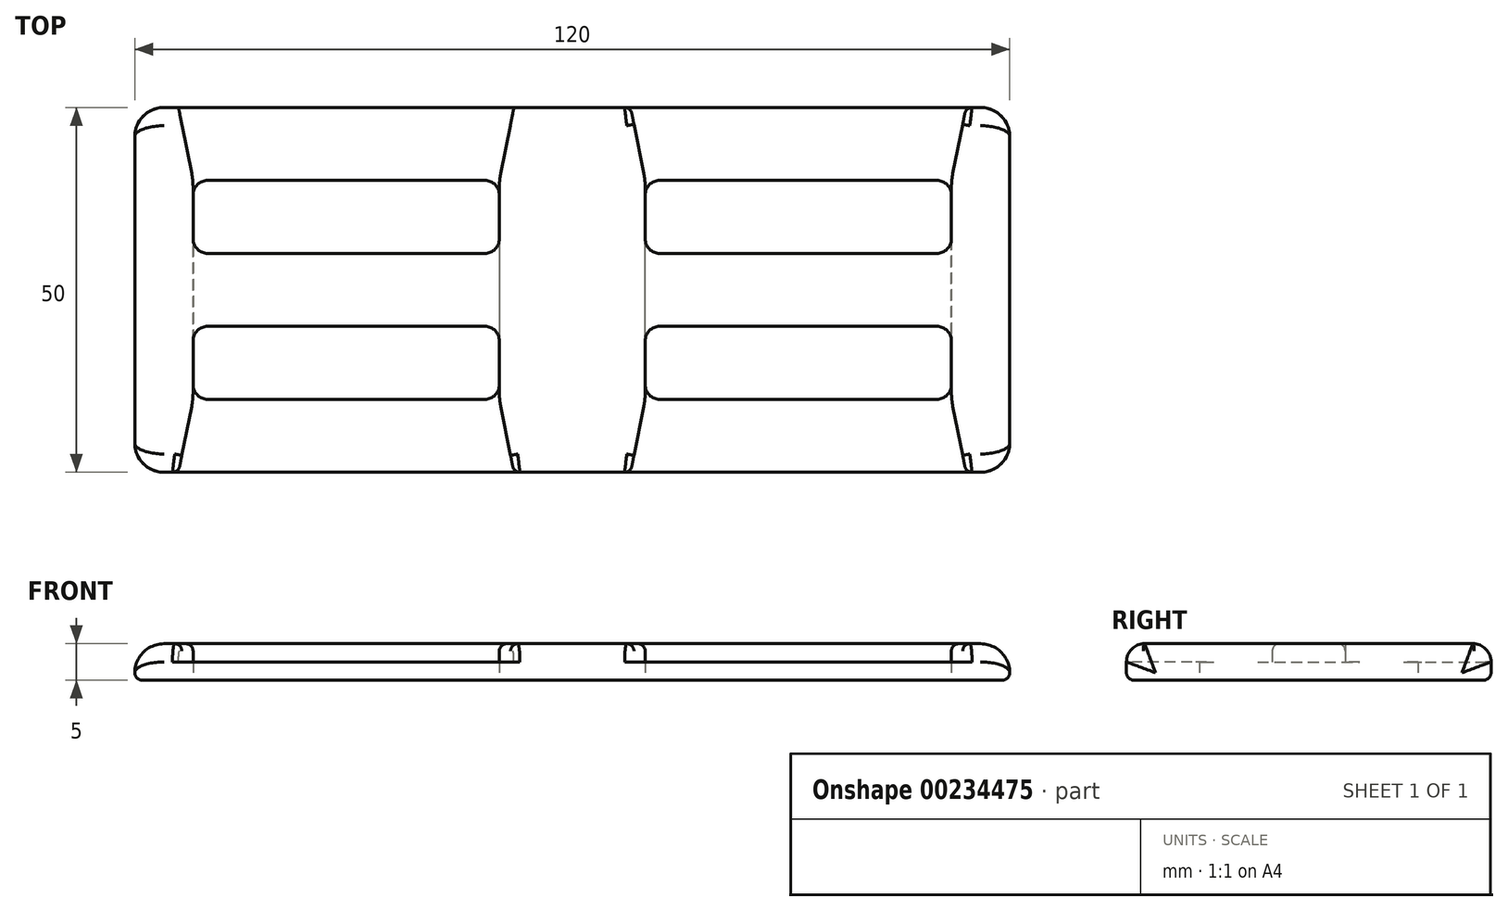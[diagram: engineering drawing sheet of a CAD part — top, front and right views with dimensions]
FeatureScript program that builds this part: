
annotation { "Feature Type Name" : "Feature", "Feature Type Description" : "" }
export const myFeature = defineFeature(function(context is Context, id is Id, definition is map)
    precondition{}
    {
        {
            var Q0;
            Q0=qCreatedBy(makeId("Top.planeOp"),FACE);
            var sketch = newSketch(context, id + "F0", { "sketchPlane" : qUnion([Q0])});
            skLineSegment(sketch, "E0.bottom", {"start": v(-60, 25) * mm, "end": v(60, 25) * mm});
            skLineSegment(sketch, "E0.top", {"start": v(-60, -25) * mm, "end": v(60, -25) * mm});
            skLineSegment(sketch, "E0.left", {"start": v(-60, 25) * mm, "end": v(-60, -25) * mm});
            skLineSegment(sketch, "E0.right", {"start": v(60, 25) * mm, "end": v(60, -25) * mm});
            skPoint(sketch, "E0.middle", {"position": v(0, 0) * mm});
            skLineSegment(sketch, "E1.bottom", {"start": v(-52, 15) * mm, "end": v(-10, 15) * mm});
            skLineSegment(sketch, "E1.top", {"start": v(-52, 5) * mm, "end": v(-10, 5) * mm});
            skLineSegment(sketch, "E1.left", {"start": v(-52, 15) * mm, "end": v(-52, 5) * mm});
            skLineSegment(sketch, "E1.right", {"start": v(-10, 15) * mm, "end": v(-10, 5) * mm});
            skLineSegment(sketch, "E2.MirrorCS", {"start": v(52, 15) * mm, "end": v(52, 5) * mm});
            skLineSegment(sketch, "E3.MirrorCS", {"start": v(52, 15) * mm, "end": v(10, 15) * mm});
            skLineSegment(sketch, "E4.MirrorCS", {"start": v(52, 5) * mm, "end": v(10, 5) * mm});
            skLineSegment(sketch, "E5.MirrorCS", {"start": v(10, 15) * mm, "end": v(10, 5) * mm});
            skLineSegment(sketch, "E6.MirrorCS", {"start": v(-52, -5) * mm, "end": v(-10, -5) * mm});
            skLineSegment(sketch, "E7.MirrorCS", {"start": v(10, -15) * mm, "end": v(10, -5) * mm});
            skLineSegment(sketch, "E8.MirrorCS", {"start": v(-52, -15) * mm, "end": v(-10, -15) * mm});
            skLineSegment(sketch, "E9.MirrorCS", {"start": v(52, -5) * mm, "end": v(10, -5) * mm});
            skLineSegment(sketch, "E10.MirrorCS", {"start": v(-52, -15) * mm, "end": v(-52, -5) * mm});
            skLineSegment(sketch, "E11.MirrorCS", {"start": v(52, -15) * mm, "end": v(10, -15) * mm});
            skLineSegment(sketch, "E12.MirrorCS", {"start": v(-10, -15) * mm, "end": v(-10, -5) * mm});
            skLineSegment(sketch, "E13.MirrorCS", {"start": v(52, -15) * mm, "end": v(52, -5) * mm});
            skSolve(sketch);
        }
        {
            var Q0;
            Q0 = qSketchRegion(id + "F0", true);
            extrude(context, id + "F1", {"entities" : qUnion([Q0]), "depth" : 5 * mm, "offsetDistance" : 25 * mm});
        }
        {
            var Q0;
            Q0=makeQuery(id+"F1.opExtrude","CAP_FACE",FACE,{"disambiguationData":[OSD([sQuery(id+"F0.wireOp",EDGE,"E0.bottom"),sQuery(id+"F0.wireOp",EDGE,"E0.top"),sQuery(id+"F0.wireOp",EDGE,"E0.left"),sQuery(id+"F0.wireOp",EDGE,"E0.right"),sQuery(id+"F0.wireOp",EDGE,"E1.bottom"),sQuery(id+"F0.wireOp",EDGE,"E1.top"),sQuery(id+"F0.wireOp",EDGE,"E1.left"),sQuery(id+"F0.wireOp",EDGE,"E1.right"),sQuery(id+"F0.wireOp",EDGE,"E2.MirrorCS"),sQuery(id+"F0.wireOp",EDGE,"E3.MirrorCS"),sQuery(id+"F0.wireOp",EDGE,"E4.MirrorCS"),sQuery(id+"F0.wireOp",EDGE,"E5.MirrorCS"),sQuery(id+"F0.wireOp",EDGE,"E6.MirrorCS"),sQuery(id+"F0.wireOp",EDGE,"E7.MirrorCS"),sQuery(id+"F0.wireOp",EDGE,"E8.MirrorCS"),sQuery(id+"F0.wireOp",EDGE,"E9.MirrorCS"),sQuery(id+"F0.wireOp",EDGE,"E10.MirrorCS"),sQuery(id+"F0.wireOp",EDGE,"E11.MirrorCS"),sQuery(id+"F0.wireOp",EDGE,"E12.MirrorCS"),sQuery(id+"F0.wireOp",EDGE,"E13.MirrorCS")])],"isStart":false});
            var sketch = newSketch(context, id + "F2", { "sketchPlane" : qUnion([Q0])});
            skLineSegment(sketch, "E14.0", {"start": v(-52, 15) * mm, "end": v(-10, 15) * mm});
            skLineSegment(sketch, "E15.0", {"start": v(-54, 25) * mm, "end": v(-8, 25) * mm});
            skLineSegment(sketch, "E16", {"start": v(-52, 15) * mm, "end": v(-54, 25) * mm});
            skLineSegment(sketch, "E17", {"start": v(-10, 15) * mm, "end": v(-8, 25) * mm});
            skLineSegment(sketch, "E18", {"start": v(-31, 15) * mm, "end": v(-31, 25) * mm, "construction": true});
            skPoint(sketch, "E19.orphan", {"position": v(60, 25) * mm});
            skPoint(sketch, "E20.orphan", {"position": v(-60, 25) * mm});
            skLineSegment(sketch, "E21.MirrorCS", {"start": v(54, 25) * mm, "end": v(8, 25) * mm});
            skLineSegment(sketch, "E22.MirrorCS", {"start": v(52, 15) * mm, "end": v(54, 25) * mm});
            skLineSegment(sketch, "E23.MirrorCS", {"start": v(52, 15) * mm, "end": v(10, 15) * mm});
            skLineSegment(sketch, "E24.MirrorCS", {"start": v(10, 15) * mm, "end": v(8, 25) * mm});
            skLineSegment(sketch, "E25.MirrorCS", {"start": v(31, 15) * mm, "end": v(31, 25) * mm, "construction": true});
            skLineSegment(sketch, "E26.MirrorCS", {"start": v(52, -15) * mm, "end": v(10, -15) * mm});
            skLineSegment(sketch, "E27.MirrorCS", {"start": v(-52, -15) * mm, "end": v(-54, -25) * mm});
            skLineSegment(sketch, "E28.MirrorCS", {"start": v(54, -25) * mm, "end": v(8, -25) * mm});
            skLineSegment(sketch, "E29.MirrorCS", {"start": v(10, -15) * mm, "end": v(8, -25) * mm});
            skPoint(sketch, "E30.MirrorP", {"position": v(60, -25) * mm});
            skLineSegment(sketch, "E31.MirrorCS", {"start": v(-54, -25) * mm, "end": v(-8, -25) * mm});
            skLineSegment(sketch, "E32.MirrorCS", {"start": v(-10, -15) * mm, "end": v(-8, -25) * mm});
            skLineSegment(sketch, "E33.MirrorCS", {"start": v(52, -15) * mm, "end": v(54, -25) * mm});
            skPoint(sketch, "E34.MirrorP", {"position": v(-60, -25) * mm});
            skLineSegment(sketch, "E35.MirrorCS", {"start": v(-52, -15) * mm, "end": v(-10, -15) * mm});
            skLineSegment(sketch, "E36.MirrorCS", {"start": v(-31, -15) * mm, "end": v(-31, -25) * mm, "construction": true});
            skLineSegment(sketch, "E37.MirrorCS", {"start": v(31, -15) * mm, "end": v(31, -25) * mm, "construction": true});
            skSolve(sketch);
        }
        {
            var Q0;
            Q0=qCreatedBy(makeId("Top.planeOp"),FACE);
            var sketch = newSketch(context, id + "F3", { "sketchPlane" : qUnion([Q0])});
            skLineSegment(sketch, "E38.0", {"start": v(-52, 5) * mm, "end": v(-10, 5) * mm});
            skLineSegment(sketch, "E39.0", {"start": v(-52, -5) * mm, "end": v(-10, -5) * mm});
            skLineSegment(sketch, "E40.0", {"start": v(52, -5) * mm, "end": v(10, -5) * mm});
            skLineSegment(sketch, "E41.0", {"start": v(52, 5) * mm, "end": v(10, 5) * mm});
            skLineSegment(sketch, "E42", {"start": v(-52, -5) * mm, "end": v(-52, 5) * mm});
            skLineSegment(sketch, "E43", {"start": v(-10, 5) * mm, "end": v(-10, -5) * mm});
            skLineSegment(sketch, "E44", {"start": v(10, -5) * mm, "end": v(10, 5) * mm});
            skLineSegment(sketch, "E45", {"start": v(52, 5) * mm, "end": v(52, -5) * mm});
            skSolve(sketch);
        }
        {
            var Q0;
            Q0 = qSketchRegion(id + "F2", true);
            extrude(context, id + "F4", {"entities" : qUnion([Q0]), "operationType" : NewBodyOperationType.REMOVE, "oppositeDirection" : true, "depth" : 2.5 * mm, "offsetDistance" : 25 * mm});
        }
        {
            var Q0;
            Q0 = qSketchRegion(id + "F3", true);
            extrude(context, id + "F5", {"entities" : qUnion([Q0]), "operationType" : NewBodyOperationType.REMOVE, "depth" : 2.5 * mm, "offsetDistance" : 25 * mm});
        }
        {
            var Q0;
            {var subQ0=sQuery(id+"F0.wireOp",EDGE,"E0.bottom");var subQ1=sQuery(id+"F0.wireOp",EDGE,"E0.right");Q0=makeQuery(id+"F4.boolean.opBoolean","SPLIT",EDGE,{"disambiguationData":[TD([makeQuery(id+"F1.opExtrude","SWEPT_FACE",FACE,{"disambiguationData":[OSD([subQ1])]})])],"derivedFrom":makeQuery(id+"F1.opExtrude","CAP_EDGE",EDGE,{"disambiguationData":[OSD([subQ0])],"isStart":false})});}
            var Q1;
            {var subQ0=sQuery(id+"F0.wireOp",EDGE,"E0.bottom");Q1=makeQuery(id+"F4.boolean.opBoolean","SPLIT",EDGE,{"disambiguationData":[TD([makeQuery(id+"F4.opExtrude","SWEPT_FACE",FACE,{"disambiguationData":[OSD([sQuery(id+"F2.wireOp",EDGE,"E17")])]})])],"derivedFrom":makeQuery(id+"F1.opExtrude","CAP_EDGE",EDGE,{"disambiguationData":[OSD([subQ0])],"isStart":false})});}
            var Q2;
            {var subQ0=sQuery(id+"F0.wireOp",EDGE,"E0.bottom");var subQ1=sQuery(id+"F0.wireOp",EDGE,"E0.left");Q2=makeQuery(id+"F4.boolean.opBoolean","SPLIT",EDGE,{"disambiguationData":[TD([makeQuery(id+"F1.opExtrude","SWEPT_FACE",FACE,{"disambiguationData":[OSD([subQ1])]})])],"derivedFrom":makeQuery(id+"F1.opExtrude","CAP_EDGE",EDGE,{"disambiguationData":[OSD([subQ0])],"isStart":false})});}
            var Q3;
            {var subQ0=sQuery(id+"F0.wireOp",EDGE,"E0.left");var subQ1=sQuery(id+"F0.wireOp",EDGE,"E0.top");Q3=makeQuery(id+"F4.boolean.opBoolean","SPLIT",EDGE,{"disambiguationData":[TD([makeQuery(id+"F1.opExtrude","SWEPT_FACE",FACE,{"disambiguationData":[OSD([subQ0])]})])],"derivedFrom":makeQuery(id+"F1.opExtrude","CAP_EDGE",EDGE,{"disambiguationData":[OSD([subQ1])],"isStart":false})});}
            var Q4;
            {var subQ0=sQuery(id+"F0.wireOp",EDGE,"E0.top");Q4=makeQuery(id+"F4.boolean.opBoolean","SPLIT",EDGE,{"disambiguationData":[TD([makeQuery(id+"F4.opExtrude","SWEPT_FACE",FACE,{"disambiguationData":[OSD([sQuery(id+"F2.wireOp",EDGE,"E29.MirrorCS")])]})])],"derivedFrom":makeQuery(id+"F1.opExtrude","CAP_EDGE",EDGE,{"disambiguationData":[OSD([subQ0])],"isStart":false})});}
            var Q5;
            {var subQ0=sQuery(id+"F0.wireOp",EDGE,"E0.right");var subQ1=sQuery(id+"F0.wireOp",EDGE,"E0.top");Q5=makeQuery(id+"F4.boolean.opBoolean","SPLIT",EDGE,{"disambiguationData":[TD([makeQuery(id+"F1.opExtrude","SWEPT_FACE",FACE,{"disambiguationData":[OSD([subQ0])]})])],"derivedFrom":makeQuery(id+"F1.opExtrude","CAP_EDGE",EDGE,{"disambiguationData":[OSD([subQ1])],"isStart":false})});}
            fillet(context, id + "F6", {"entities" : qUnion([Q0, Q1, Q2, Q3, Q4, Q5]), "tangentPropagation" : true, "radius" : 2.5 * mm, "defaultsChanged" : false, "vertexSettings" : [], "allowEdgeOverflow" : false});
        }
        {
            var Q0;
            Q0=makeQuery(id+"F1.opExtrude","CAP_EDGE",EDGE,{"disambiguationData":[OSD([sQuery(id+"F0.wireOp",EDGE,"E0.right")])],"isStart":false});
            var Q1;
            Q1=makeQuery(id+"F1.opExtrude","CAP_EDGE",EDGE,{"disambiguationData":[OSD([sQuery(id+"F0.wireOp",EDGE,"E0.left")])],"isStart":false});
            fillet(context, id + "F7", {"entities" : qUnion([Q0, Q1]), "tangentPropagation" : true, "radius" : 4 * mm, "defaultsChanged" : false, "vertexSettings" : [], "allowEdgeOverflow" : false});
        }
        {
            var Q0;
            Q0=makeQuery(id+"F1.opExtrude","SWEPT_EDGE",EDGE,{"disambiguationData":[OSD([sQuery(id+"F0.wireOp",EDGE,"E2.MirrorCS"),sQuery(id+"F0.wireOp",EDGE,"E4.MirrorCS")])]});
            var Q1;
            Q1=makeQuery(id+"F1.opExtrude","SWEPT_EDGE",EDGE,{"disambiguationData":[OSD([sQuery(id+"F0.wireOp",EDGE,"E4.MirrorCS"),sQuery(id+"F0.wireOp",EDGE,"E5.MirrorCS")])]});
            var Q2;
            Q2=makeQuery(id+"F1.opExtrude","SWEPT_EDGE",EDGE,{"disambiguationData":[OSD([sQuery(id+"F0.wireOp",EDGE,"E1.top"),sQuery(id+"F0.wireOp",EDGE,"E1.right")])]});
            var Q3;
            Q3=makeQuery(id+"F1.opExtrude","SWEPT_EDGE",EDGE,{"disambiguationData":[OSD([sQuery(id+"F0.wireOp",EDGE,"E1.top"),sQuery(id+"F0.wireOp",EDGE,"E1.left")])]});
            var Q4;
            Q4=makeQuery(id+"F4.boolean.opBoolean","SPLIT",EDGE,{"derivedFrom":makeQuery(id+"F1.opExtrude","SWEPT_EDGE",EDGE,{"disambiguationData":[OSD([sQuery(id+"F0.wireOp",EDGE,"E8.MirrorCS"),sQuery(id+"F0.wireOp",EDGE,"E10.MirrorCS")])]})});
            var Q5;
            Q5=makeQuery(id+"F4.boolean.opBoolean","SPLIT",EDGE,{"derivedFrom":makeQuery(id+"F1.opExtrude","SWEPT_EDGE",EDGE,{"disambiguationData":[OSD([sQuery(id+"F0.wireOp",EDGE,"E8.MirrorCS"),sQuery(id+"F0.wireOp",EDGE,"E12.MirrorCS")])]})});
            var Q6;
            Q6=makeQuery(id+"F4.boolean.opBoolean","SPLIT",EDGE,{"derivedFrom":makeQuery(id+"F1.opExtrude","SWEPT_EDGE",EDGE,{"disambiguationData":[OSD([sQuery(id+"F0.wireOp",EDGE,"E11.MirrorCS"),sQuery(id+"F0.wireOp",EDGE,"E13.MirrorCS")])]})});
            var Q7;
            Q7=makeQuery(id+"F4.boolean.opBoolean","SPLIT",EDGE,{"derivedFrom":makeQuery(id+"F1.opExtrude","SWEPT_EDGE",EDGE,{"disambiguationData":[OSD([sQuery(id+"F0.wireOp",EDGE,"E7.MirrorCS"),sQuery(id+"F0.wireOp",EDGE,"E11.MirrorCS")])]})});
            var Q8;
            Q8=makeQuery(id+"F1.opExtrude","SWEPT_EDGE",EDGE,{"disambiguationData":[OSD([sQuery(id+"F0.wireOp",EDGE,"E6.MirrorCS"),sQuery(id+"F0.wireOp",EDGE,"E12.MirrorCS")])]});
            var Q9;
            Q9=makeQuery(id+"F1.opExtrude","SWEPT_EDGE",EDGE,{"disambiguationData":[OSD([sQuery(id+"F0.wireOp",EDGE,"E6.MirrorCS"),sQuery(id+"F0.wireOp",EDGE,"E10.MirrorCS")])]});
            var Q10;
            Q10=makeQuery(id+"F1.opExtrude","SWEPT_EDGE",EDGE,{"disambiguationData":[OSD([sQuery(id+"F0.wireOp",EDGE,"E7.MirrorCS"),sQuery(id+"F0.wireOp",EDGE,"E9.MirrorCS")])]});
            var Q11;
            Q11=makeQuery(id+"F1.opExtrude","SWEPT_EDGE",EDGE,{"disambiguationData":[OSD([sQuery(id+"F0.wireOp",EDGE,"E9.MirrorCS"),sQuery(id+"F0.wireOp",EDGE,"E13.MirrorCS")])]});
            var Q12;
            Q12=makeQuery(id+"F4.boolean.opBoolean","SPLIT",EDGE,{"derivedFrom":makeQuery(id+"F1.opExtrude","SWEPT_EDGE",EDGE,{"disambiguationData":[OSD([sQuery(id+"F0.wireOp",EDGE,"E2.MirrorCS"),sQuery(id+"F0.wireOp",EDGE,"E3.MirrorCS")])]})});
            var Q13;
            Q13=makeQuery(id+"F4.boolean.opBoolean","SPLIT",EDGE,{"derivedFrom":makeQuery(id+"F1.opExtrude","SWEPT_EDGE",EDGE,{"disambiguationData":[OSD([sQuery(id+"F0.wireOp",EDGE,"E3.MirrorCS"),sQuery(id+"F0.wireOp",EDGE,"E5.MirrorCS")])]})});
            var Q14;
            Q14=makeQuery(id+"F4.boolean.opBoolean","SPLIT",EDGE,{"derivedFrom":makeQuery(id+"F1.opExtrude","SWEPT_EDGE",EDGE,{"disambiguationData":[OSD([sQuery(id+"F0.wireOp",EDGE,"E1.bottom"),sQuery(id+"F0.wireOp",EDGE,"E1.left")])]})});
            var Q15;
            Q15=makeQuery(id+"F4.boolean.opBoolean","SPLIT",EDGE,{"derivedFrom":makeQuery(id+"F1.opExtrude","SWEPT_EDGE",EDGE,{"disambiguationData":[OSD([sQuery(id+"F0.wireOp",EDGE,"E1.bottom"),sQuery(id+"F0.wireOp",EDGE,"E1.right")])]})});
            fillet(context, id + "F8", {"entities" : qUnion([Q0, Q1, Q2, Q3, Q4, Q5, Q6, Q7, Q8, Q9, Q10, Q11, Q12, Q13, Q14, Q15]), "tangentPropagation" : true, "radius" : 2 * mm, "defaultsChanged" : false, "vertexSettings" : [], "allowEdgeOverflow" : false});
        }
        {
            var Q0;
            {var subQ0=sQuery(id+"F0.wireOp",EDGE,"E2.MirrorCS");Q0=makeQuery(id+"F4.boolean.opBoolean","MERGE",EDGE,{"derivedFrom":[makeQuery(id+"F1.opExtrude","SWEPT_EDGE",EDGE,{"disambiguationData":[OSD([subQ0,sQuery(id+"F0.wireOp",EDGE,"E3.MirrorCS")])]})],"fromTools":[makeQuery(id+"F4.opExtrude","SWEPT_EDGE",EDGE,{"disambiguationData":[OSD([subQ0,sQuery(id+"F2.wireOp",EDGE,"E22.MirrorCS"),sQuery(id+"F2.wireOp",EDGE,"E23.MirrorCS")])]})]});}
            var Q1;
            {var subQ0=sQuery(id+"F0.wireOp",EDGE,"E5.MirrorCS");Q1=makeQuery(id+"F4.boolean.opBoolean","MERGE",EDGE,{"derivedFrom":[makeQuery(id+"F1.opExtrude","SWEPT_EDGE",EDGE,{"disambiguationData":[OSD([sQuery(id+"F0.wireOp",EDGE,"E3.MirrorCS"),subQ0])]})],"fromTools":[makeQuery(id+"F4.opExtrude","SWEPT_EDGE",EDGE,{"disambiguationData":[OSD([subQ0,sQuery(id+"F2.wireOp",EDGE,"E23.MirrorCS"),sQuery(id+"F2.wireOp",EDGE,"E24.MirrorCS")])]})]});}
            var Q2;
            {var subQ0=sQuery(id+"F0.wireOp",EDGE,"E1.right");Q2=makeQuery(id+"F4.boolean.opBoolean","MERGE",EDGE,{"derivedFrom":[makeQuery(id+"F1.opExtrude","SWEPT_EDGE",EDGE,{"disambiguationData":[OSD([sQuery(id+"F0.wireOp",EDGE,"E1.bottom"),subQ0])]})],"fromTools":[makeQuery(id+"F4.opExtrude","SWEPT_EDGE",EDGE,{"disambiguationData":[OSD([subQ0,sQuery(id+"F2.wireOp",EDGE,"E14.0"),sQuery(id+"F2.wireOp",EDGE,"E17")])]})]});}
            var Q3;
            {var subQ0=sQuery(id+"F0.wireOp",EDGE,"E1.left");Q3=makeQuery(id+"F4.boolean.opBoolean","MERGE",EDGE,{"derivedFrom":[makeQuery(id+"F1.opExtrude","SWEPT_EDGE",EDGE,{"disambiguationData":[OSD([sQuery(id+"F0.wireOp",EDGE,"E1.bottom"),subQ0])]})],"fromTools":[makeQuery(id+"F4.opExtrude","SWEPT_EDGE",EDGE,{"disambiguationData":[OSD([subQ0,sQuery(id+"F2.wireOp",EDGE,"E14.0"),sQuery(id+"F2.wireOp",EDGE,"E16")])]})]});}
            var Q4;
            {var subQ0=sQuery(id+"F0.wireOp",EDGE,"E10.MirrorCS");Q4=makeQuery(id+"F4.boolean.opBoolean","MERGE",EDGE,{"derivedFrom":[makeQuery(id+"F1.opExtrude","SWEPT_EDGE",EDGE,{"disambiguationData":[OSD([sQuery(id+"F0.wireOp",EDGE,"E8.MirrorCS"),subQ0])]})],"fromTools":[makeQuery(id+"F4.opExtrude","SWEPT_EDGE",EDGE,{"disambiguationData":[OSD([subQ0,sQuery(id+"F2.wireOp",EDGE,"E27.MirrorCS"),sQuery(id+"F2.wireOp",EDGE,"E35.MirrorCS")])]})]});}
            var Q5;
            {var subQ0=sQuery(id+"F0.wireOp",EDGE,"E7.MirrorCS");Q5=makeQuery(id+"F4.boolean.opBoolean","MERGE",EDGE,{"derivedFrom":[makeQuery(id+"F1.opExtrude","SWEPT_EDGE",EDGE,{"disambiguationData":[OSD([subQ0,sQuery(id+"F0.wireOp",EDGE,"E11.MirrorCS")])]})],"fromTools":[makeQuery(id+"F4.opExtrude","SWEPT_EDGE",EDGE,{"disambiguationData":[OSD([subQ0,sQuery(id+"F2.wireOp",EDGE,"E26.MirrorCS"),sQuery(id+"F2.wireOp",EDGE,"E29.MirrorCS")])]})]});}
            var Q6;
            {var subQ0=sQuery(id+"F0.wireOp",EDGE,"E13.MirrorCS");Q6=makeQuery(id+"F4.boolean.opBoolean","MERGE",EDGE,{"derivedFrom":[makeQuery(id+"F1.opExtrude","SWEPT_EDGE",EDGE,{"disambiguationData":[OSD([sQuery(id+"F0.wireOp",EDGE,"E11.MirrorCS"),subQ0])]})],"fromTools":[makeQuery(id+"F4.opExtrude","SWEPT_EDGE",EDGE,{"disambiguationData":[OSD([subQ0,sQuery(id+"F2.wireOp",EDGE,"E26.MirrorCS"),sQuery(id+"F2.wireOp",EDGE,"E33.MirrorCS")])]})]});}
            var Q7;
            {var subQ0=sQuery(id+"F0.wireOp",EDGE,"E12.MirrorCS");Q7=makeQuery(id+"F4.boolean.opBoolean","MERGE",EDGE,{"derivedFrom":[makeQuery(id+"F1.opExtrude","SWEPT_EDGE",EDGE,{"disambiguationData":[OSD([sQuery(id+"F0.wireOp",EDGE,"E8.MirrorCS"),subQ0])]})],"fromTools":[makeQuery(id+"F4.opExtrude","SWEPT_EDGE",EDGE,{"disambiguationData":[OSD([subQ0,sQuery(id+"F2.wireOp",EDGE,"E32.MirrorCS"),sQuery(id+"F2.wireOp",EDGE,"E35.MirrorCS")])]})]});}
            fillet(context, id + "F9", {"entities" : qUnion([Q0, Q1, Q2, Q3, Q4, Q5, Q6, Q7]), "tangentPropagation" : true, "radius" : 10 * mm, "defaultsChanged" : false, "vertexSettings" : [], "allowEdgeOverflow" : false});
        }
        {
            var Q0;
            {var subQ0=makeQuery(id+"F4.opExtrude","SWEPT_FACE",FACE,{"disambiguationData":[OSD([sQuery(id+"F2.wireOp",EDGE,"E22.MirrorCS")])]});var subQ1=sQuery(id+"F0.wireOp",EDGE,"E0.bottom");var subQ2=sQuery(id+"F0.wireOp",EDGE,"E0.right");Q0=makeQuery(id+"F6.opFillet","BLEND_EDGE",EDGE,{"blendedFrom":[makeQuery(id+"F4.boolean.opBoolean","SPLIT",EDGE,{"disambiguationData":[TD([makeQuery(id+"F1.opExtrude","SWEPT_FACE",FACE,{"disambiguationData":[OSD([subQ2])]})])],"derivedFrom":makeQuery(id+"F1.opExtrude","CAP_EDGE",EDGE,{"disambiguationData":[OSD([subQ1])],"isStart":false})}),makeQuery(id+"F4.boolean.opBoolean","COPY",FACE,{"derivedFrom":subQ0})],"blendedInto":[makeQuery(id+"F4.boolean.opBoolean","COPY",FACE,{"derivedFrom":subQ0})]});}
            var Q1;
            Q1=makeQuery(id+"F4.boolean.opBoolean","COPY",EDGE,{"derivedFrom":makeQuery(id+"F4.opExtrude","CAP_EDGE",EDGE,{"disambiguationData":[OSD([sQuery(id+"F2.wireOp",EDGE,"E23.MirrorCS")])],"isStart":false})});
            var Q2;
            Q2=makeQuery(id+"F4.boolean.opBoolean","COPY",EDGE,{"derivedFrom":makeQuery(id+"F4.opExtrude","CAP_EDGE",EDGE,{"disambiguationData":[OSD([sQuery(id+"F2.wireOp",EDGE,"E17")])],"isStart":true})});
            var Q3;
            Q3=makeQuery(id+"F4.boolean.opBoolean","COPY",EDGE,{"derivedFrom":makeQuery(id+"F4.opExtrude","CAP_EDGE",EDGE,{"disambiguationData":[OSD([sQuery(id+"F2.wireOp",EDGE,"E14.0")])],"isStart":false})});
            var Q4;
            Q4=makeQuery(id+"F4.boolean.opBoolean","COPY",EDGE,{"derivedFrom":makeQuery(id+"F4.opExtrude","CAP_EDGE",EDGE,{"disambiguationData":[OSD([sQuery(id+"F2.wireOp",EDGE,"E35.MirrorCS")])],"isStart":false})});
            var Q5;
            Q5=makeQuery(id+"F1.opExtrude","CAP_EDGE",EDGE,{"disambiguationData":[OSD([sQuery(id+"F0.wireOp",EDGE,"E12.MirrorCS")])],"isStart":false});
            var Q6;
            Q6=makeQuery(id+"F4.boolean.opBoolean","COPY",EDGE,{"derivedFrom":makeQuery(id+"F4.opExtrude","CAP_EDGE",EDGE,{"disambiguationData":[OSD([sQuery(id+"F2.wireOp",EDGE,"E26.MirrorCS")])],"isStart":false})});
            var Q7;
            Q7=makeQuery(id+"F1.opExtrude","CAP_EDGE",EDGE,{"disambiguationData":[OSD([sQuery(id+"F0.wireOp",EDGE,"E13.MirrorCS")])],"isStart":false});
            var Q8;
            Q8=makeQuery(id+"F5.boolean.opBoolean","COPY",EDGE,{"derivedFrom":makeQuery(id+"F5.opExtrude","CAP_EDGE",EDGE,{"disambiguationData":[OSD([sQuery(id+"F3.wireOp",EDGE,"E41.0")])],"isStart":false})});
            var Q9;
            Q9=makeQuery(id+"F5.boolean.opBoolean","COPY",EDGE,{"derivedFrom":makeQuery(id+"F5.opExtrude","CAP_EDGE",EDGE,{"disambiguationData":[OSD([sQuery(id+"F3.wireOp",EDGE,"E40.0")])],"isStart":false})});
            var Q10;
            Q10=makeQuery(id+"F5.boolean.opBoolean","COPY",EDGE,{"derivedFrom":makeQuery(id+"F5.opExtrude","CAP_EDGE",EDGE,{"disambiguationData":[OSD([sQuery(id+"F3.wireOp",EDGE,"E39.0")])],"isStart":false})});
            var Q11;
            Q11=makeQuery(id+"F5.boolean.opBoolean","COPY",EDGE,{"derivedFrom":makeQuery(id+"F5.opExtrude","CAP_EDGE",EDGE,{"disambiguationData":[OSD([sQuery(id+"F3.wireOp",EDGE,"E38.0")])],"isStart":false})});
            var Q12;
            Q12=makeQuery(id+"F1.opExtrude","CAP_EDGE",EDGE,{"disambiguationData":[OSD([sQuery(id+"F0.wireOp",EDGE,"E0.bottom")])],"isStart":true});
            var Q13;
            Q13=makeQuery(id+"F5.boolean.opBoolean","MERGE",EDGE,{"derivedFrom":[makeQuery(id+"F1.opExtrude","CAP_EDGE",EDGE,{"disambiguationData":[OSD([sQuery(id+"F0.wireOp",EDGE,"E2.MirrorCS")])],"isStart":true}),makeQuery(id+"F1.opExtrude","CAP_EDGE",EDGE,{"disambiguationData":[OSD([sQuery(id+"F0.wireOp",EDGE,"E13.MirrorCS")])],"isStart":true})],"fromTools":[makeQuery(id+"F5.opExtrude","CAP_EDGE",EDGE,{"disambiguationData":[OSD([sQuery(id+"F3.wireOp",EDGE,"E45")])],"isStart":true})]});
            var Q14;
            Q14=makeQuery(id+"F5.boolean.opBoolean","MERGE",EDGE,{"derivedFrom":[makeQuery(id+"F1.opExtrude","CAP_EDGE",EDGE,{"disambiguationData":[OSD([sQuery(id+"F0.wireOp",EDGE,"E1.right")])],"isStart":true}),makeQuery(id+"F1.opExtrude","CAP_EDGE",EDGE,{"disambiguationData":[OSD([sQuery(id+"F0.wireOp",EDGE,"E12.MirrorCS")])],"isStart":true})],"fromTools":[makeQuery(id+"F5.opExtrude","CAP_EDGE",EDGE,{"disambiguationData":[OSD([sQuery(id+"F3.wireOp",EDGE,"E43")])],"isStart":true})]});
            fillet(context, id + "F10", {"entities" : qUnion([Q0, Q1, Q2, Q3, Q4, Q5, Q6, Q7, Q8, Q9, Q10, Q11, Q12, Q13, Q14]), "tangentPropagation" : true, "radius" : 1 * mm, "defaultsChanged" : false, "vertexSettings" : [], "allowEdgeOverflow" : false});
        }
    });
